# Revit family: equip-faucet-elkay-lk810-GN
name_source: partatom
category: Plumbing Fixtures
units: mm (PartAtom-declared; Revit-internal decimal feet)

## family parameters
Always vertical = Yes
Cut with Voids When Loaded = No
OmniClass Number = 23.45.55.17
OmniClass Title = Mixing Faucets
Part Type = Normal
Room Calculation Point = No
Round Connector Dimension = Use Radius
Shared = No
Work Plane-Based = No

## types (1)
- ByType
    Assembly Code = D2010900
    CW Flow Rate = 2 GPM
    Cost = 0 $
    Description = LK810 Series Deck Mount Faucets
    Faucet Material = Metal - Steel - Stainless - Chrome
    GN04 = No
    GN05 = No
    GN08 = No
    HW Flow Rate = 2 GPM
    L2 = No
    Manufacturer = Elkay Manufacturing
    MasterFormat Number = 22 42 39
    MasterFormat Title = Commercial Faucet
    Model = LK810
    Nominal Dia = 0' - 0 1/2"
    Nominal Radius = 0' - 0 1/4"
    OmniClass Code = 23.45.55.17
    OmniClass Title = Mixing Faucets
    SideSpray = No
    Stem Material = Metal - Steel
    T4 = No
    T6 = No
    URL = www.elkayusa.com

## geometry (parser evidence)
native form markers: Sweep x2
no freeform markers — native parametric forms only
